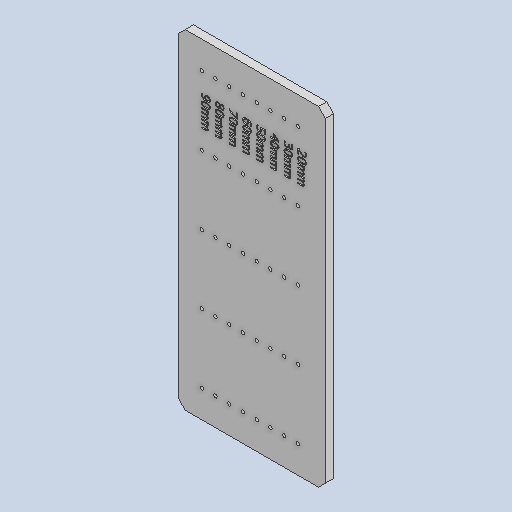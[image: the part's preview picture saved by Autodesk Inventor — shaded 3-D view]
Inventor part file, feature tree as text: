
AUTODESK INVENTOR PART (.ipt)
format: ipt  version: 2022 (Build 260153000, 153)  size: 1,295,360 bytes
history: native  units: mm
features: sketch x3, other x3, extrude x2, reference x2, projected_geometry x2, chamfer x1, pattern_linear x1, emboss x1
ambient origin geometry x8: Origin, YZ Plane, XZ Plane, XY Plane, X Axis, Y Axis, Z Axis, Center Point
bodies: Solid1 (feature_tree)
feature tree (15):
  extrude  "Extrusion1"  Depth=6.0mm TaperAngle=0.0deg
  extrude  "Extrusion2"  Depth=2.5mm
  chamfer  "Chamfer1"  Distance=2.5mm
  pattern_linear  "Rectangular Pattern1"  Spacing1=2.5mm  [1 undecoded]
  emboss  "Emboss1"
  sketch  "Sketch1"  dims[d6=20.0mm d7=6.0mm d8=0.0mm]
  reference  "Reference1"
  sketch  "Sketch3"  dims[d9=80.0mm d10=2.5mm]
  reference  "Reference2"
  sketch  "Sketch4"  dims[d11=2.5mm d12=2.5mm d13=2.5mm d14=2.5mm d15=0.0mm d16=0.0mm d17=80.0mm d19=10.0mm d20=20.0mm d21=1.0mm d22=0.0mm d23=5.0mm d24=2.0mm d25=45.0deg]
  projected_geometry  "Projected Loop1"
  projected_geometry  "Projected Loop2"
  other  "<userpath>\Desktop\Storage-Rack\A.iam"
  other  "A.iam"
  other  "A-00:1"
note: 1 required parameter value undecoded (feature->parameter linkage not recoverable at this tier; creation-order binding heuristic only, values carry confidence <= 0.55)
